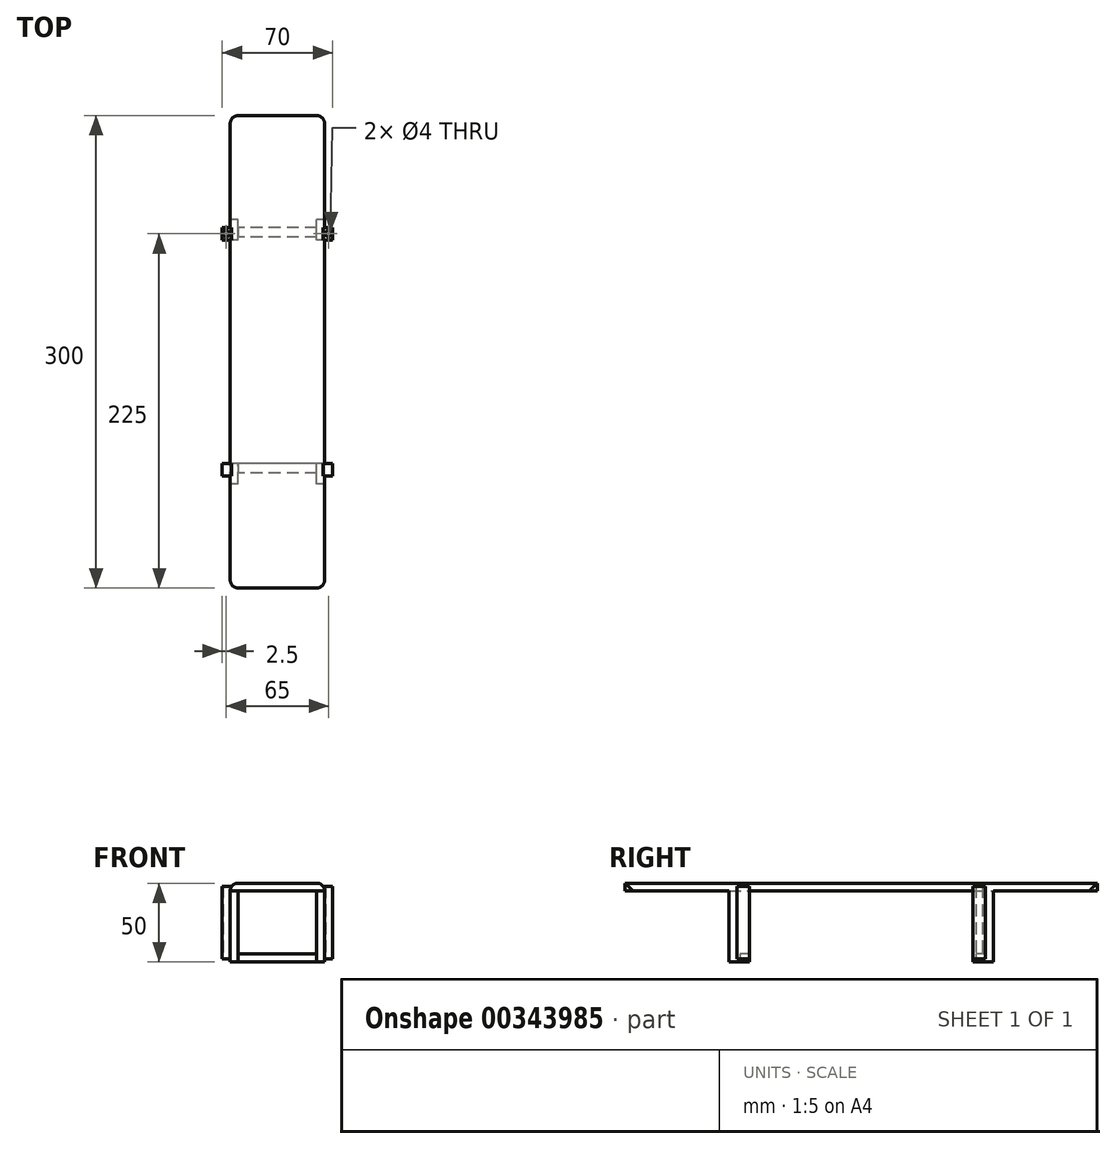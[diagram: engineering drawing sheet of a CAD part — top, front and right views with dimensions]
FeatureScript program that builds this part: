
annotation { "Feature Type Name" : "Feature", "Feature Type Description" : "" }
export const myFeature = defineFeature(function(context is Context, id is Id, definition is map)
    precondition{}
    {
        {
            var Q0;
            Q0=qCreatedBy(makeId("Front.planeOp"),FACE);
            var sketch = newSketch(context, id + "F0", { "sketchPlane" : qUnion([Q0])});
            skLineSegment(sketch, "E0.bottom", {"start": v(0, 0) * mm, "end": v(60, 0) * mm});
            skLineSegment(sketch, "E0.top", {"start": v(0, 50) * mm, "end": v(60, 50) * mm});
            skLineSegment(sketch, "E0.left", {"start": v(0, 0) * mm, "end": v(0, 50) * mm});
            skLineSegment(sketch, "E0.right", {"start": v(60, 0) * mm, "end": v(60, 50) * mm});
            skSolve(sketch);
        }
        {
            var Q0;
            Q0=makeQuery(id+"F0.imprint","IMPRINT",FACE,{"disambiguationData":[TD([[makeQuery(id+"F0.imprint","IMPRINT",EDGE,{"derivedFrom":sQuery(id+"F0.wireOp",EDGE,"E0.bottom")}),1.0]])]});
            var sketch = newSketch(context, id + "F1", { "sketchPlane" : qUnion([Q0])});
            skLineSegment(sketch, "E1.bottom", {"start": v(5, 0) * mm, "end": v(55, 0) * mm});
            skLineSegment(sketch, "E1.top", {"start": v(5, 45) * mm, "end": v(55, 45) * mm});
            skLineSegment(sketch, "E1.left", {"start": v(5, 0) * mm, "end": v(5, 45) * mm});
            skLineSegment(sketch, "E1.right", {"start": v(55, 0) * mm, "end": v(55, 45) * mm});
            skSolve(sketch);
        }
        {
            var Q0;
            Q0=makeQuery(id+"F1.imprint","IMPRINT",FACE,{"disambiguationData":[TD([[makeQuery(id+"F1.imprint","IMPRINT",EDGE,{"derivedFrom":sQuery(id+"F1.wireOp",EDGE,"E1.top")}),1.0]])]});
            extrude(context, id + "F2", {"entities" : qUnion([Q0]), "depth" : 300 * mm});
        }
        {
            var Q0;
            Q0=makeQuery(id+"F2.opExtrude","SWEPT_FACE",FACE,{"disambiguationData":[OSD([sQuery(id+"F0.wireOp",EDGE,"E0.right")])]});
            var sketch = newSketch(context, id + "F3", { "sketchPlane" : qUnion([Q0])});
            skLineSegment(sketch, "E2", {"start": v(-150, 50) * mm, "end": v(-150, 0) * mm, "construction": true});
            skLineSegment(sketch, "E3", {"start": v(-225, 50) * mm, "end": v(-225, 0) * mm, "construction": true});
            skLineSegment(sketch, "E4", {"start": v(-75, 50) * mm, "end": v(-75, 0) * mm, "construction": true});
            skLineSegment(sketch, "E5.bottom", {"start": v(-229, 48) * mm, "end": v(-221, 48) * mm});
            skLineSegment(sketch, "E5.top", {"start": v(-229, 2) * mm, "end": v(-221, 2) * mm});
            skLineSegment(sketch, "E5.left", {"start": v(-229, 48) * mm, "end": v(-229, 2) * mm});
            skLineSegment(sketch, "E5.right", {"start": v(-221, 48) * mm, "end": v(-221, 2) * mm});
            skLineSegment(sketch, "E6.bottom", {"start": v(-79, 48) * mm, "end": v(-71, 48) * mm});
            skLineSegment(sketch, "E6.top", {"start": v(-79, 2) * mm, "end": v(-71, 2) * mm});
            skLineSegment(sketch, "E6.left", {"start": v(-79, 48) * mm, "end": v(-79, 2) * mm});
            skLineSegment(sketch, "E6.right", {"start": v(-71, 48) * mm, "end": v(-71, 2) * mm});
            skSolve(sketch);
        }
        {
            var Q0;
            Q0=makeQuery(id+"F3.imprint","IMPRINT",FACE,{"disambiguationData":[TD([[makeQuery(id+"F3.imprint","IMPRINT",EDGE,{"derivedFrom":sQuery(id+"F3.wireOp",EDGE,"E5.bottom")}),-1.0]])]});
            var Q1;
            Q1=makeQuery(id+"F3.imprint","IMPRINT",FACE,{"disambiguationData":[TD([[makeQuery(id+"F3.imprint","IMPRINT",EDGE,{"derivedFrom":sQuery(id+"F3.wireOp",EDGE,"E6.bottom")}),-1.0]])]});
            extrude(context, id + "F4", {"entities" : qUnion([Q0, Q1]), "operationType" : NewBodyOperationType.ADD, "depth" : 5 * mm});
        }
        {
            var Q0;
            Q0=makeQuery(id+"F2.opExtrude","SWEPT_FACE",FACE,{"disambiguationData":[OSD([sQuery(id+"F0.wireOp",EDGE,"E0.left")])]});
            var sketch = newSketch(context, id + "F5", { "sketchPlane" : qUnion([Q0])});
            skLineSegment(sketch, "E7", {"start": v(150, 50) * mm, "end": v(150, 0) * mm, "construction": true});
            skLineSegment(sketch, "E8", {"start": v(75, 50) * mm, "end": v(75, 0) * mm, "construction": true});
            skLineSegment(sketch, "E9", {"start": v(225, 50) * mm, "end": v(225, 0) * mm, "construction": true});
            skLineSegment(sketch, "E10.bottom", {"start": v(71, 48) * mm, "end": v(79, 48) * mm});
            skLineSegment(sketch, "E10.top", {"start": v(71, 2) * mm, "end": v(79, 2) * mm});
            skLineSegment(sketch, "E10.left", {"start": v(71, 48) * mm, "end": v(71, 2) * mm});
            skLineSegment(sketch, "E10.right", {"start": v(79, 48) * mm, "end": v(79, 2) * mm});
            skLineSegment(sketch, "E11.bottom", {"start": v(221, 48) * mm, "end": v(229, 48) * mm});
            skLineSegment(sketch, "E11.top", {"start": v(221, 2) * mm, "end": v(229, 2) * mm});
            skLineSegment(sketch, "E11.left", {"start": v(221, 48) * mm, "end": v(221, 2) * mm});
            skLineSegment(sketch, "E11.right", {"start": v(229, 48) * mm, "end": v(229, 2) * mm});
            skSolve(sketch);
        }
        {
            var Q0;
            Q0=makeQuery(id+"F5.imprint","IMPRINT",FACE,{"disambiguationData":[TD([[makeQuery(id+"F5.imprint","IMPRINT",EDGE,{"derivedFrom":sQuery(id+"F5.wireOp",EDGE,"E10.bottom")}),-1.0]])]});
            var Q1;
            Q1=makeQuery(id+"F5.imprint","IMPRINT",FACE,{"disambiguationData":[TD([[makeQuery(id+"F5.imprint","IMPRINT",EDGE,{"derivedFrom":sQuery(id+"F5.wireOp",EDGE,"E11.bottom")}),-1.0]])]});
            extrude(context, id + "F6", {"entities" : qUnion([Q0, Q1]), "operationType" : NewBodyOperationType.ADD, "depth" : 5 * mm});
        }
        {
            var Q0;
            {var subQ0=sQuery(id+"F0.wireOp",EDGE,"E0.bottom");var subQ1=makeQuery(id+"F0.imprint","IMPRINT",EDGE,{"derivedFrom":subQ0});Q0=makeQuery(id+"F2.opExtrude","SWEPT_FACE",FACE,{"disambiguationData":[OSD([subQ0]),TDD([makeQuery(id+"F1.imprint","IMPRINT",EDGE,{"disambiguationData":[TD([[makeQuery(id+"F1.imprint","INTERSECT",VERTEX,{"derivedFrom":[subQ1,makeQuery(id+"F0.imprint","IMPRINT",EDGE,{"derivedFrom":sQuery(id+"F0.wireOp",EDGE,"E0.right")})]}),1.0]])],"derivedFrom":subQ1})])]});}
            var sketch = newSketch(context, id + "F7", { "sketchPlane" : qUnion([Q0])});
            skLineSegment(sketch, "E12.bottom", {"start": v(55, 71) * mm, "end": v(5, 71) * mm});
            skLineSegment(sketch, "E12.top", {"start": v(55, 77) * mm, "end": v(5, 77) * mm});
            skLineSegment(sketch, "E12.left", {"start": v(55, 71) * mm, "end": v(55, 77) * mm});
            skLineSegment(sketch, "E12.right", {"start": v(5, 71) * mm, "end": v(5, 77) * mm});
            skLineSegment(sketch, "E13.bottom", {"start": v(55, 221) * mm, "end": v(5, 221) * mm});
            skLineSegment(sketch, "E13.top", {"start": v(55, 227) * mm, "end": v(5, 227) * mm});
            skLineSegment(sketch, "E13.left", {"start": v(55, 221) * mm, "end": v(55, 227) * mm});
            skLineSegment(sketch, "E13.right", {"start": v(5, 221) * mm, "end": v(5, 227) * mm});
            skSolve(sketch);
        }
        {
            var Q0;
            Q0=makeQuery(id+"F7.imprint","IMPRINT",FACE,{"disambiguationData":[TD([[makeQuery(id+"F7.imprint","IMPRINT",EDGE,{"derivedFrom":sQuery(id+"F7.wireOp",EDGE,"E12.bottom")}),-1.0]])]});
            var Q1;
            Q1=makeQuery(id+"F7.imprint","IMPRINT",FACE,{"disambiguationData":[TD([[makeQuery(id+"F7.imprint","IMPRINT",EDGE,{"derivedFrom":sQuery(id+"F7.wireOp",EDGE,"E13.bottom")}),-1.0]])]});
            extrude(context, id + "F8", {"entities" : qUnion([Q0, Q1]), "operationType" : NewBodyOperationType.ADD, "oppositeDirection" : true, "depth" : 5 * mm});
        }
        {
            var Q0;
            Q0=makeQuery(id+"F2.opExtrude","SWEPT_FACE",FACE,{"disambiguationData":[OSD([sQuery(id+"F0.wireOp",EDGE,"E0.left")])]});
            var sketch = newSketch(context, id + "F9", { "sketchPlane" : qUnion([Q0])});
            skLineSegment(sketch, "E14.bottom", {"start": v(79, 45) * mm, "end": v(221, 45) * mm});
            skLineSegment(sketch, "E14.top", {"start": v(79, 0) * mm, "end": v(221, 0) * mm});
            skLineSegment(sketch, "E14.left", {"start": v(79, 45) * mm, "end": v(79, 0) * mm});
            skLineSegment(sketch, "E14.right", {"start": v(221, 45) * mm, "end": v(221, 0) * mm});
            skLineSegment(sketch, "E15.bottom", {"start": v(66, 45) * mm, "end": v(0, 45) * mm});
            skLineSegment(sketch, "E15.top", {"start": v(66, 0) * mm, "end": v(0, 0) * mm});
            skLineSegment(sketch, "E15.left", {"start": v(66, 45) * mm, "end": v(66, 0) * mm});
            skLineSegment(sketch, "E15.right", {"start": v(0, 45) * mm, "end": v(0, 0) * mm});
            skLineSegment(sketch, "E16.bottom", {"start": v(300, 45) * mm, "end": v(234, 45) * mm});
            skLineSegment(sketch, "E16.top", {"start": v(300, 0) * mm, "end": v(234, 0) * mm});
            skLineSegment(sketch, "E16.left", {"start": v(300, 45) * mm, "end": v(300, 0) * mm});
            skLineSegment(sketch, "E16.right", {"start": v(234, 45) * mm, "end": v(234, 0) * mm});
            skSolve(sketch);
        }
        {
            var Q0;
            Q0=makeQuery(id+"F9.imprint","IMPRINT",FACE,{"disambiguationData":[TD([[makeQuery(id+"F9.imprint","IMPRINT",EDGE,{"derivedFrom":sQuery(id+"F9.wireOp",EDGE,"E14.bottom")}),-1.0]])]});
            var Q1;
            Q1=makeQuery(id+"F9.imprint","IMPRINT",FACE,{"disambiguationData":[TD([[makeQuery(id+"F9.imprint","IMPRINT",EDGE,{"derivedFrom":sQuery(id+"F9.wireOp",EDGE,"E15.bottom")}),1.0]])]});
            var Q2;
            Q2=makeQuery(id+"F9.imprint","IMPRINT",FACE,{"disambiguationData":[TD([[makeQuery(id+"F9.imprint","IMPRINT",EDGE,{"derivedFrom":sQuery(id+"F9.wireOp",EDGE,"E16.bottom")}),1.0]])]});
            extrude(context, id + "F10", {"entities" : qUnion([Q0, Q1, Q2]), "operationType" : NewBodyOperationType.REMOVE, "endBound" : BoundingType.THROUGH_ALL, "oppositeDirection" : true, "depth" : 25 * mm});
        }
        {
            var Q0;
            Q0=qCreatedBy(makeId("Top.planeOp"),FACE);
            var sketch = newSketch(context, id + "F11", { "sketchPlane" : qUnion([Q0])});
            skCircle(sketch, "E17", {"center": v(-2.5, -75) * mm, "radius": 2 * mm});
            skCircle(sketch, "E18", {"center": v(62.5, -75) * mm, "radius": 2 * mm});
            skLineSegment(sketch, "E19", {"start": v(-46.92, -150) * mm, "end": v(101.44, -150) * mm, "construction": true});
            skCircle(sketch, "E20.MirrorC", {"center": v(62.5, -225) * mm, "radius": 2 * mm});
            skCircle(sketch, "E21.MirrorC", {"center": v(-2.5, -225) * mm, "radius": 2 * mm});
            skSolve(sketch);
        }
        {
            var Q0;
            Q0=makeQuery(id+"F11.imprint","IMPRINT",FACE,{"disambiguationData":[TD([[makeQuery(id+"F11.imprint","IMPRINT",EDGE,{"derivedFrom":sQuery(id+"F11.wireOp",EDGE,"E17")}),1.0]])]});
            var Q1;
            Q1=makeQuery(id+"F11.imprint","IMPRINT",FACE,{"disambiguationData":[TD([[makeQuery(id+"F11.imprint","IMPRINT",EDGE,{"derivedFrom":sQuery(id+"F11.wireOp",EDGE,"E18")}),1.0]])]});
            var Q2;
            Q2=makeQuery(id+"F11.imprint","IMPRINT",FACE,{"disambiguationData":[TD([[makeQuery(id+"F11.imprint","IMPRINT",EDGE,{"derivedFrom":sQuery(id+"F11.wireOp",EDGE,"E21.MirrorC")}),-1.0]])]});
            var Q3;
            Q3=makeQuery(id+"F11.imprint","IMPRINT",FACE,{"disambiguationData":[TD([[makeQuery(id+"F11.imprint","IMPRINT",EDGE,{"derivedFrom":sQuery(id+"F11.wireOp",EDGE,"E20.MirrorC")}),-1.0]])]});
            extrude(context, id + "F12", {"entities" : qUnion([Q0, Q1, Q2, Q3]), "operationType" : NewBodyOperationType.REMOVE, "endBound" : BoundingType.THROUGH_ALL, "depth" : 25 * mm});
        }
        {
            var Q0;
            Q0=makeQuery(id+"F2.opExtrude","SWEPT_EDGE",EDGE,{"disambiguationData":[OSD([sQuery(id+"F0.wireOp",EDGE,"E0.top"),sQuery(id+"F0.wireOp",EDGE,"E0.left")])]});
            var Q1;
            Q1=makeQuery(id+"F2.opExtrude","SWEPT_EDGE",EDGE,{"disambiguationData":[OSD([sQuery(id+"F0.wireOp",EDGE,"E0.top"),sQuery(id+"F0.wireOp",EDGE,"E0.right")])]});
            var Q2;
            Q2=makeQuery(id+"F2.opExtrude","CAP_EDGE",EDGE,{"disambiguationData":[OSD([sQuery(id+"F0.wireOp",EDGE,"E0.left")])],"isStart":false});
            var Q3;
            Q3=makeQuery(id+"F2.opExtrude","CAP_EDGE",EDGE,{"disambiguationData":[OSD([sQuery(id+"F0.wireOp",EDGE,"E0.right")])],"isStart":false});
            var Q4;
            Q4=makeQuery(id+"F2.opExtrude","CAP_EDGE",EDGE,{"disambiguationData":[OSD([sQuery(id+"F0.wireOp",EDGE,"E0.right")])],"isStart":true});
            var Q5;
            Q5=makeQuery(id+"F2.opExtrude","CAP_EDGE",EDGE,{"disambiguationData":[OSD([sQuery(id+"F0.wireOp",EDGE,"E0.left")])],"isStart":true});
            fillet(context, id + "F13", {"entities" : qUnion([Q0, Q1, Q2, Q3, Q4, Q5]), "radius" : 5 * mm, "tangentPropagation" : true, "allowEdgeOverflow" : false});
        }
    });
